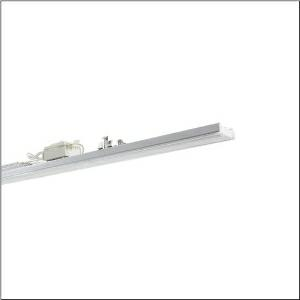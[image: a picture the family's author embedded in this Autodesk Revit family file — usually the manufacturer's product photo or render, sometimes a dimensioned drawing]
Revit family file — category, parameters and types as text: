
# Revit family: licross_r__21_recessed_mo_52te12dv4fxg3s_e0fc
name_source: partatom
category: Lighting Fixtures
units: mm (PartAtom-declared; Revit-internal decimal feet)

## family parameters
Cut with Voids When Loaded = No
Host = Face
Light Source = No
Part Type = Normal
Room Calculation Point = No
Round Connector Dimension = Use Diameter
Shared = No

## types (1)
- --- (1 x LED, 950 lm, 5.5 W, 4000K)
    Apparent Load = 6 VA
    CIE Flux Codes = 72 92 99 100 100
    Color Rendering = 80
    Color Temperature = 4000K
    Default Elevation = 1800 mm
    Description = Licross® 21 Recessed MO, luminaire insert, of sheet steel, galvanised, coil coated, white, length: 2.250mm, width: 66mm, height: 67mm, LED rated luminous flux: 15.420lm, light colour: 840, control gear: DALI 2 (for two DALI lines), with plug, 6-pole, with phase selection, for trunking rail, 14-core, mains connection: 220..240V, AC, 50/60Hz, rated input power: 89W, for trunking rail, 14-core, internal wiring halogen-free, for emergency light function, converter,control gear: single battery element, battery: LiFePO4, 9Ah, primary optical cover: cover, of PMMA, light emission: direct distribution, primary light characteristic: symmetric, protection rating (complete): IP54, insulation class (complete): insulation class I (protective earthing), certification: CE, UKCA, protection symbol: D if used in an environment with non-conductive dust loads with corresponding accessories, impact resistance: IK06, permissible ambient temperature for indoor applications: +5..+35°C, standard: EN 60598-2-22, LABS conformity tested according to VDMA 24364:2018-05, reducing of maximum allowable ambient temperature of 5°C with ceiling mounting, corresponds to IFS (International Featured Standards) requirements for safety and quality in the food industry, packaging unit: 1 piece
    Height = 58 mm
    Lamp = 1 x LED
    Lamp Light Flux = 950 lm
    Lamp Power = 5.5 W
    Lamp count = 1
    Length = 2250 mm
    Luminous efficacy = 173 lm/W
    Manufacturer = Siteco
    ModVariant = No
    Model = 52TE12DV4FXG3S
    Mounting Place = Ceiling
    Mounting Type = Pendant
    Number of Poles = 1
    OnlyDefault = Yes
    Power Factor = 1
    Product Name = Licross® 21 Recessed MO
    Product group = luminaire insert | ceiling pendant
    ProductGroupID = 902
    Protection Class = Protection class I
    Protection Degree = IP 54
    RLX_Detail_Level = 1
    RLX_Emergency_Light_Flux = 0 lm
    RLX_Emergency_Type = 0
    RLX_Emergency_Type_DB = No
    RlxData = <blob elided: 30077 chars, md5=7852e523>
    Socket = socket
    Standby Power = 0 W
    System Light Flux = 950 lm
    System Power = 6 W
    Type Comments = : emergency light operation: 3 h
    Type Image = l_1296930.jpg
    URL = http://relux.com
    VarID = @adj_131547
    Voltage = 0 V
    Weight = 0.00 kg
    Width = 66 mm

## geometry (parser evidence)
native form markers: Blend x4, Sweep x9
no freeform markers — native parametric forms only
